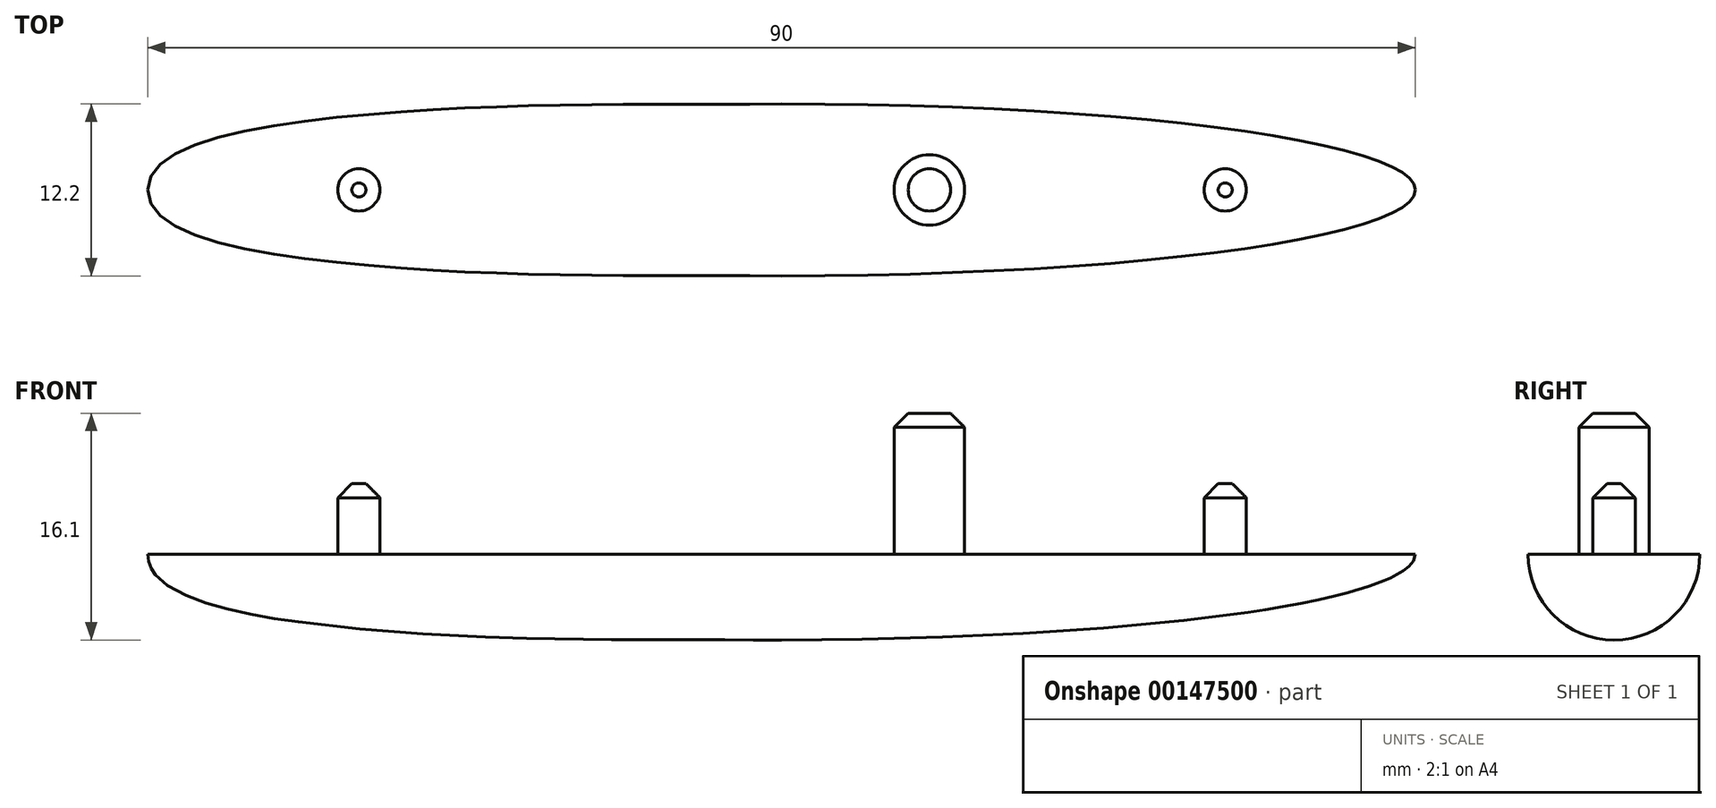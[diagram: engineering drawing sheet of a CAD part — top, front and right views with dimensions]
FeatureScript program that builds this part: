
annotation { "Feature Type Name" : "Feature", "Feature Type Description" : "" }
export const myFeature = defineFeature(function(context is Context, id is Id, definition is map)
    precondition{}
    {
        {
            var Q0;
            Q0=qCreatedBy(makeId("Top.planeOp"),FACE);
            var sketch = newSketch(context, id + "F0", { "sketchPlane" : qUnion([Q0])});
            skCircle(sketch, "E0", {"center": v(0, 0) * mm, "radius": 2.5 * mm, "construction": true});
            skCircle(sketch, "E1", {"center": v(-40.5, 0) * mm, "radius": 1.5 * mm, "construction": true});
            skCircle(sketch, "E2", {"center": v(21, 0) * mm, "radius": 1.5 * mm, "construction": true});
            skPoint(sketch, "E3", {"position": v(-55.5, 0) * mm});
            skPoint(sketch, "E4", {"position": v(34.5, 0) * mm});
            skLineSegment(sketch, "E5", {"start": v(-55.5, 0) * mm, "end": v(34.5, 0) * mm});
            skPoint(sketch, "E6", {"position": v(-10.5, 0) * mm});
            skPoint(sketch, "E7", {"position": v(-20.5, 0) * mm});
            skPoint(sketch, "E8", {"position": v(-30.5, 0) * mm});
            skPoint(sketch, "E9", {"position": v(-50.5, 0) * mm});
            skPoint(sketch, "E10", {"position": v(-0.5, 0) * mm});
            skPoint(sketch, "E11", {"position": v(9.5, 0) * mm});
            skPoint(sketch, "E12", {"position": v(19.5, 0) * mm});
            skPoint(sketch, "E13", {"position": v(29.5, 0) * mm});
            skPoint(sketch, "E14", {"position": v(-50.5, 4.27) * mm});
            skPoint(sketch, "E15", {"position": v(-40.5, 5.3) * mm});
            skPoint(sketch, "E16", {"position": v(-30.5, 5.72) * mm});
            skPoint(sketch, "E17", {"position": v(-20.5, 6.05) * mm});
            skPoint(sketch, "E18", {"position": v(-0.5, 6) * mm});
            skPoint(sketch, "E19", {"position": v(9.5, 5.55) * mm});
            skPoint(sketch, "E20", {"position": v(19.5, 4.8) * mm});
            skPoint(sketch, "E21", {"position": v(29.5, 3.1) * mm});
            skPoint(sketch, "E22", {"position": v(-10.5, 6.1) * mm});
            skEllipticalArc(sketch, "E23", {});
            skPoint(sketch, "E24", {"position": v(-10.5, -6.1) * mm});
            skFitSpline(sketch, "E25", {"points": [v(-55.5, 0) * mm, v(-40.5, 5.3) * mm, v(-10.5, 6.1) * mm], "startDerivative": vector(0, 23.74) * mm, "endDerivative": vector(51.84, 0.26) * mm});
            const initialGuessF0  = {"E23": [-0.0105, 0, -1, 0, 0.045, 0.0061, 3.141592653589793, 4.71238898038469]};
            skSetInitialGuess(sketch, initialGuessF0);
            skSolve(sketch);
        }
        {
            var Q0;
            Q0=qCreatedBy(makeId("Top.planeOp"),FACE);
            var sketch = newSketch(context, id + "F1", { "sketchPlane" : qUnion([Q0])});
            skCircle(sketch, "E26.0", {"center": v(-40.5, 0) * mm, "radius": 1.5 * mm});
            skCircle(sketch, "E27.0", {"center": v(0, 0) * mm, "radius": 2.5 * mm});
            skCircle(sketch, "E28.0", {"center": v(21, 0) * mm, "radius": 1.5 * mm});
            skSolve(sketch);
        }
        {
            var Q0;
            Q0=makeQuery(id+"F1.imprint","IMPRINT",FACE,{"disambiguationData":[TD([[makeQuery(id+"F1.imprint","IMPRINT",EDGE,{"derivedFrom":sQuery(id+"F1.wireOp",EDGE,"E26.0")}),1.0]])]});
            var Q1;
            Q1=makeQuery(id+"F1.imprint","IMPRINT",FACE,{"disambiguationData":[TD([[makeQuery(id+"F1.imprint","IMPRINT",EDGE,{"derivedFrom":sQuery(id+"F1.wireOp",EDGE,"E28.0")}),1.0]])]});
            extrude(context, id + "F2", {"entities" : qUnion([Q0, Q1]), "depth" : 5 * mm});
        }
        {
            var Q0;
            Q0=makeQuery(id+"F1.imprint","IMPRINT",FACE,{"disambiguationData":[TD([[makeQuery(id+"F1.imprint","IMPRINT",EDGE,{"derivedFrom":sQuery(id+"F1.wireOp",EDGE,"E27.0")}),1.0]])]});
            extrude(context, id + "F3", {"entities" : qUnion([Q0]), "depth" : 10 * mm});
        }
        {
            var Q0;
            Q0=makeQuery(id+"F2.opExtrude","CAP_EDGE",EDGE,{"disambiguationData":[OSD([sQuery(id+"F1.wireOp",EDGE,"E26.0")])],"isStart":false});
            var Q1;
            Q1=makeQuery(id+"F2.opExtrude","CAP_EDGE",EDGE,{"disambiguationData":[OSD([sQuery(id+"F1.wireOp",EDGE,"E28.0")])],"isStart":false});
            chamfer(context, id + "F4", {"entities" : qUnion([Q0, Q1]), "width" : 1 * mm, "tangentPropagation" : true});
        }
        {
            var Q0;
            Q0=makeQuery(id+"F3.opExtrude","CAP_EDGE",EDGE,{"disambiguationData":[OSD([sQuery(id+"F1.wireOp",EDGE,"E27.0")])],"isStart":false});
            chamfer(context, id + "F5", {"entities" : qUnion([Q0]), "width" : 1 * mm, "tangentPropagation" : true});
        }
        {
            var Q0;
            Q0=makeQuery(id+"F0.imprint","IMPRINT",FACE,{"disambiguationData":[TD([[makeQuery(id+"F0.imprint","IMPRINT",EDGE,{"derivedFrom":sQuery(id+"F0.wireOp",EDGE,"E5")}),1.0]])]});
            var Q1;
            Q1=sQuery(id+"F0.wireOp",EDGE,"E5");
            revolve(context, id + "F6", {"entities" : qUnion([Q0]), "axis" : qUnion([Q1]), "revolveType" : RevolveType.ONE_DIRECTION, "oppositeDirection" : true, "angle" : 180 * degree});
        }
    });
